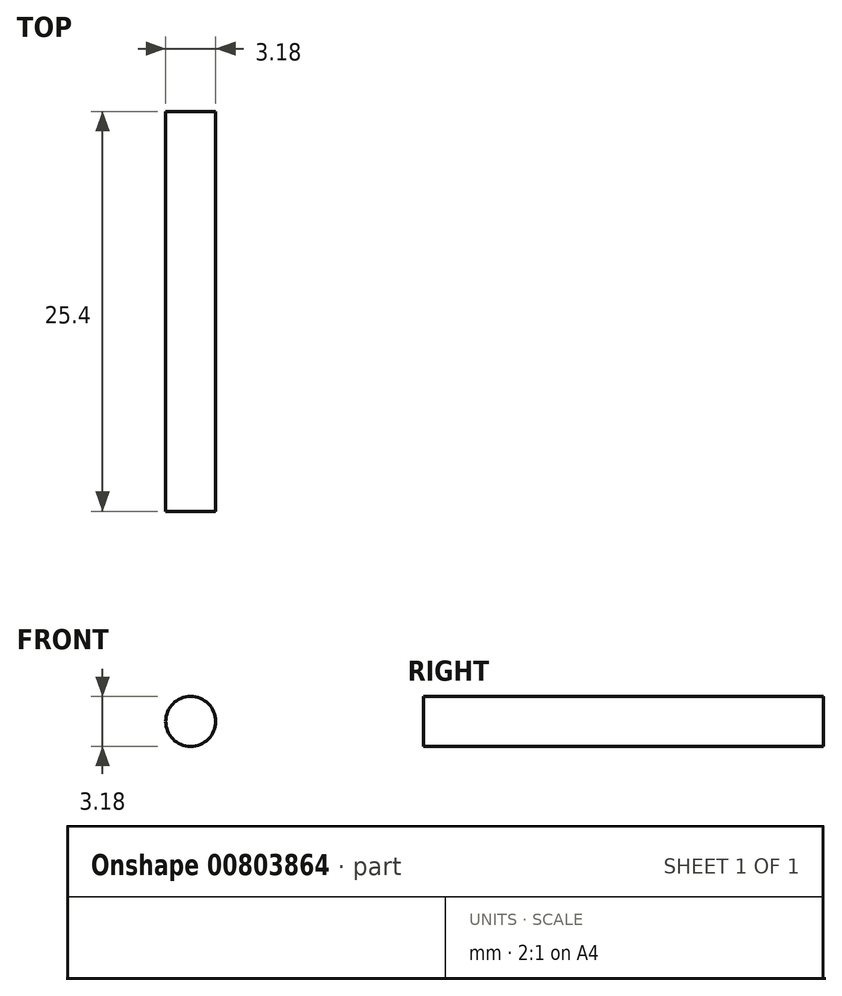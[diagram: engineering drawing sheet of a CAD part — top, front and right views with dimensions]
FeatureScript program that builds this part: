
annotation { "Feature Type Name" : "Feature", "Feature Type Description" : "" }
export const myFeature = defineFeature(function(context is Context, id is Id, definition is map)
    precondition{}
    {
        {
            var Q0;
            Q0=qCreatedBy(makeId("Front.planeOp"),FACE);
            var sketch = newSketch(context, id + "F0", { "sketchPlane" : qUnion([Q0])});
            skCircle(sketch, "E0", {"center": v(0, 0) * mm, "radius": 1.59 * mm});
            skSolve(sketch);
        }
        {
            var Q0;
            Q0=makeQuery(id+"F0.imprint","IMPRINT",FACE,{"disambiguationData":[TD([[makeQuery(id+"F0.imprint","IMPRINT",EDGE,{"derivedFrom":sQuery(id+"F0.wireOp",EDGE,"E0")}),1.0]])]});
            extrude(context, id + "F1", {"entities" : qUnion([Q0]), "depth" : 25.4 * mm, "offsetDistance" : 25.4 * mm});
        }
    });
